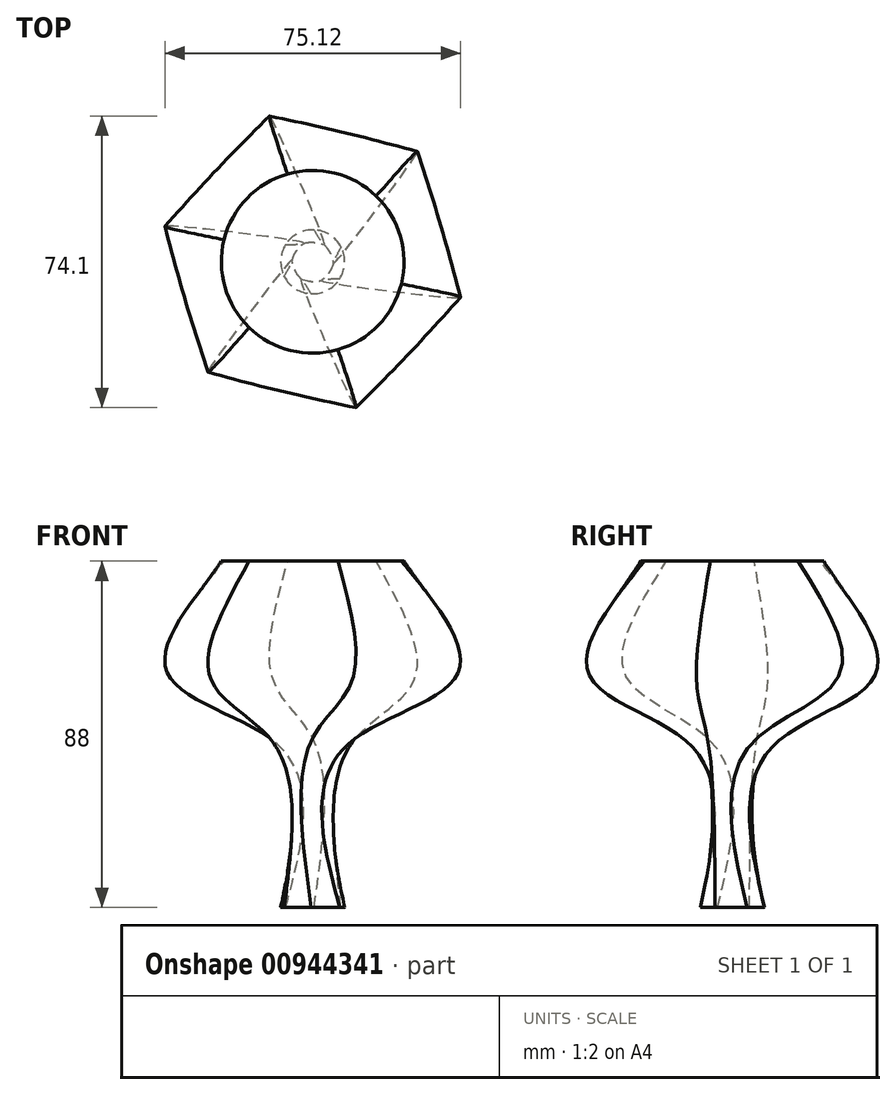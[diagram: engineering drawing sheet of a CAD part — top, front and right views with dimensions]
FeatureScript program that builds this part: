
annotation { "Feature Type Name" : "Feature", "Feature Type Description" : "" }
export const myFeature = defineFeature(function(context is Context, id is Id, definition is map)
    precondition{}
    {
        {
            var Q0;
            Q0=qCreatedBy(makeId("Top.planeOp"),FACE);
            var sketch = newSketch(context, id + "F0", { "sketchPlane" : qUnion([Q0])});
            skCircle(sketch, "E0", {"center": v(0, 0) * mm, "radius": 8.13 * mm});
            skSolve(sketch);
        }
        {
            var Q0;
            Q0=qCreatedBy(makeId("Top.planeOp"),FACE);
            cPlane(context, id + "F1", {"entities" : qUnion([Q0]), "cplaneType" : CPlaneType.OFFSET, "offset" : 88 * mm, "width" : 150 * mm, "height" : 150 * mm});
        }
        {
            var Q0;
            Q0=qCreatedBy(id+"F1.planeOp",FACE);
            var sketch = newSketch(context, id + "F2", { "sketchPlane" : qUnion([Q0])});
            skCircle(sketch, "E1", {"center": v(0, 0) * mm, "radius": 23.22 * mm});
            skSolve(sketch);
        }
        {
            var Q0;
            Q0=qCreatedBy(makeId("Top.planeOp"),FACE);
            cPlane(context, id + "F3", {"entities" : qUnion([Q0]), "cplaneType" : CPlaneType.OFFSET, "offset" : 42 * mm, "width" : 150 * mm, "height" : 150 * mm});
        }
        {
            var Q0;
            Q0=qCreatedBy(makeId("Top.planeOp"),FACE);
            cPlane(context, id + "F4", {"entities" : qUnion([Q0]), "cplaneType" : CPlaneType.OFFSET, "offset" : 59 * mm, "width" : 150 * mm, "height" : 150 * mm});
        }
        {
            var Q0;
            Q0=qCreatedBy(id+"F3.planeOp",FACE);
            var sketch = newSketch(context, id + "F5", { "sketchPlane" : qUnion([Q0])});
            skCircle(sketch, "E2.cCircle", {"center": v(0, 0) * mm, "radius": 9.85 * mm, "construction": true});
            skLineSegment(sketch, "E2.0", {"start": v(9.58, -6.13) * mm, "end": v(-0.52, -11.36) * mm});
            skLineSegment(sketch, "E2.1", {"start": v(-0.52, -11.36) * mm, "end": v(-10.1, -5.23) * mm});
            skLineSegment(sketch, "E2.2", {"start": v(-10.1, -5.23) * mm, "end": v(-9.58, 6.13) * mm});
            skLineSegment(sketch, "E2.3", {"start": v(-9.58, 6.13) * mm, "end": v(0.52, 11.36) * mm});
            skLineSegment(sketch, "E2.4", {"start": v(0.52, 11.36) * mm, "end": v(10.1, 5.23) * mm});
            skLineSegment(sketch, "E2.5", {"start": v(10.1, 5.23) * mm, "end": v(9.58, -6.13) * mm});
            skPoint(sketch, "E2.0.midPoint", {"position": v(4.53, -8.75) * mm});
            skSolve(sketch);
        }
        {
            var Q0;
            Q0=qCreatedBy(id+"F4.planeOp",FACE);
            var sketch = newSketch(context, id + "F6", { "sketchPlane" : qUnion([Q0])});
            skCircle(sketch, "E3.cCircle", {"center": v(0, 0) * mm, "radius": 32.7 * mm, "construction": true});
            skLineSegment(sketch, "E3.0", {"start": v(-10.41, 36.29) * mm, "end": v(26.22, 27.16) * mm});
            skLineSegment(sketch, "E3.1", {"start": v(26.22, 27.16) * mm, "end": v(36.63, -9.13) * mm});
            skLineSegment(sketch, "E3.2", {"start": v(36.63, -9.13) * mm, "end": v(10.41, -36.29) * mm});
            skLineSegment(sketch, "E3.3", {"start": v(10.41, -36.29) * mm, "end": v(-26.22, -27.16) * mm});
            skLineSegment(sketch, "E3.4", {"start": v(-26.22, -27.16) * mm, "end": v(-36.63, 9.13) * mm});
            skLineSegment(sketch, "E3.5", {"start": v(-36.63, 9.13) * mm, "end": v(-10.41, 36.29) * mm});
            skPoint(sketch, "E3.0.midPoint", {"position": v(7.9, 31.72) * mm});
            skSolve(sketch);
        }
        {
            var Q0;
            Q0=makeQuery(id+"F0.imprint","IMPRINT",FACE,{"disambiguationData":[TD([[makeQuery(id+"F0.imprint","IMPRINT",EDGE,{"derivedFrom":sQuery(id+"F0.wireOp",EDGE,"E0")}),1.0]])]});
            var Q1;
            Q1=makeQuery(id+"F5.imprint","IMPRINT",FACE,{"disambiguationData":[TD([[makeQuery(id+"F5.imprint","IMPRINT",EDGE,{"derivedFrom":sQuery(id+"F5.wireOp",EDGE,"E2.0")}),-1.0]])]});
            var Q2;
            Q2=makeQuery(id+"F6.imprint","IMPRINT",FACE,{"disambiguationData":[TD([[makeQuery(id+"F6.imprint","IMPRINT",EDGE,{"derivedFrom":sQuery(id+"F6.wireOp",EDGE,"E3.0")}),-1.0]])]});
            var Q3;
            Q3=makeQuery(id+"F2.imprint","IMPRINT",FACE,{"disambiguationData":[TD([[makeQuery(id+"F2.imprint","IMPRINT",EDGE,{"derivedFrom":sQuery(id+"F2.wireOp",EDGE,"E1")}),1.0]])]});
            loft(context, id + "F7", {"sheetProfilesArray" : [{ "sheetProfileEntities" : qUnion([Q0]) }, { "sheetProfileEntities" : qUnion([Q1]) }, { "sheetProfileEntities" : qUnion([Q2]) }, { "sheetProfileEntities" : qUnion([Q3]) }]});
        }
    });
